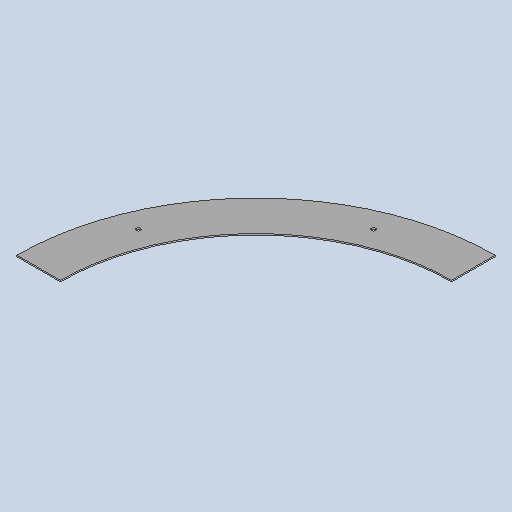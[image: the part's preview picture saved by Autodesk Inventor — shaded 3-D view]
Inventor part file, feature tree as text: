
AUTODESK INVENTOR PART (.ipt)
format: ipt  version: 2025 (Build 290162010, 162A)  size: 129,536 bytes
history: native  units: mm
features: other x3, sketch x2, sheet_metal_op x1, pattern_circular x1
ambient origin geometry x8: Origin, YZ Plane, XZ Plane, XY Plane, X Axis, Y Axis, Z Axis, Center Point
bodies: Solid1 (feature_tree)
feature tree (7):
  sheet_metal_op  "Face1"
  pattern_circular  "Circular Pattern1"  Count=110  [1 undecoded]
  sketch  "Sketch1"  dims[d1=900.0mm]
  other  "Plate1"
  sketch  "Sketch2"  dims[d2=3.0mm d4=10.0mm d5=22.5deg d6=3.0mm d7=0.0mm d8=20.0mm d9=45.0deg]
  other  "Cut1"
  other  "Definition1"
note: 1 required parameter value undecoded (feature->parameter linkage not recoverable at this tier; creation-order binding heuristic only, values carry confidence <= 0.55)
